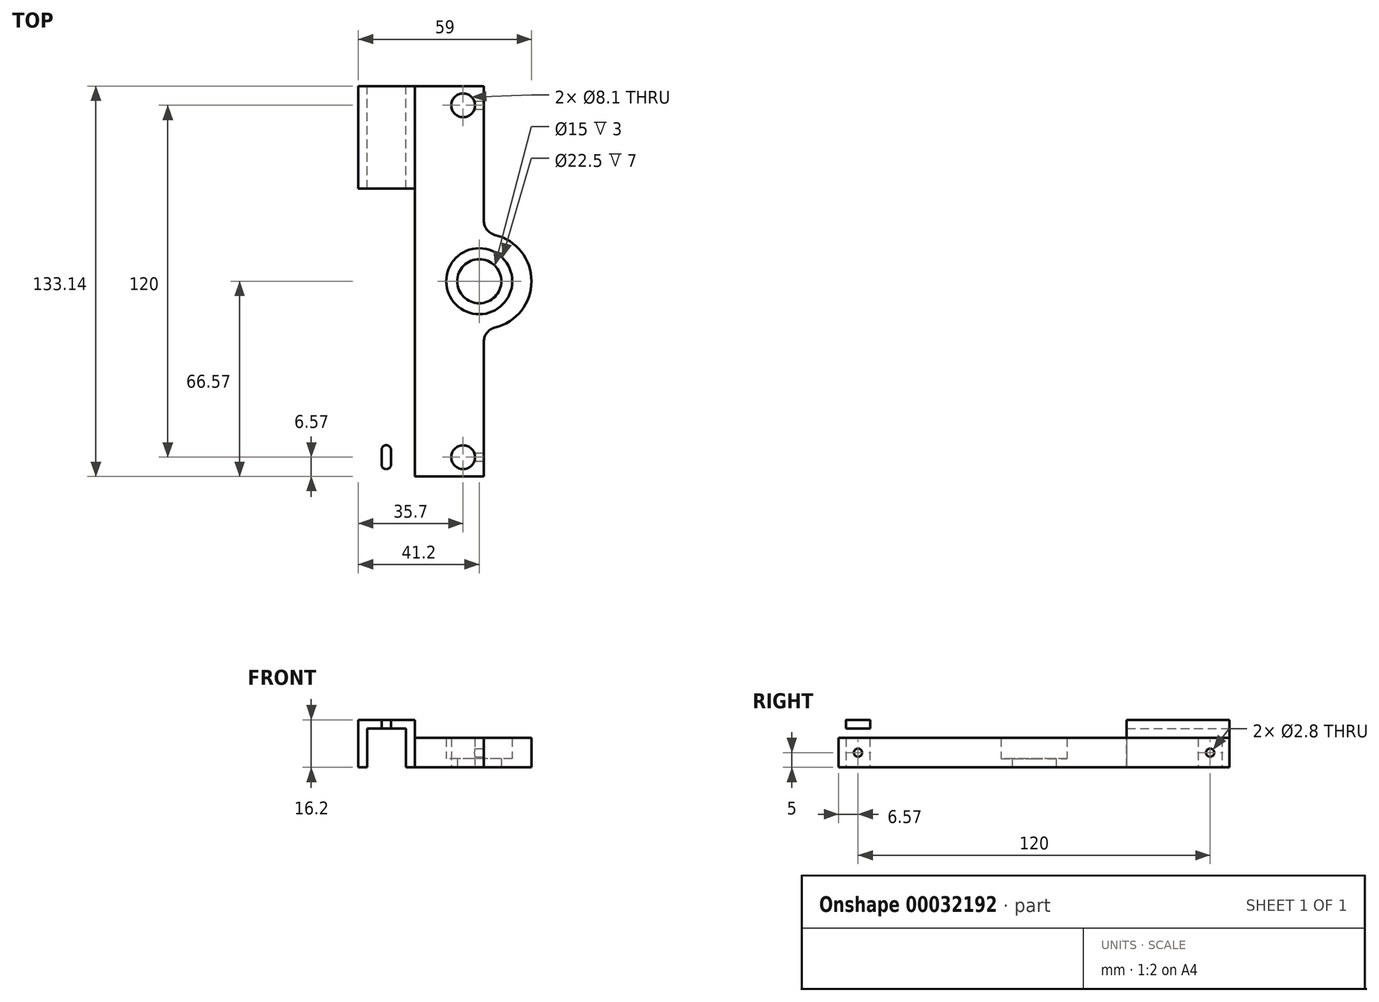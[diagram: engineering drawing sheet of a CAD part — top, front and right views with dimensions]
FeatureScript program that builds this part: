
annotation { "Feature Type Name" : "Feature", "Feature Type Description" : "" }
export const myFeature = defineFeature(function(context is Context, id is Id, definition is map)
    precondition{}
    {
        {
            var Q0;
            Q0=qCreatedBy(makeId("Top.planeOp"),FACE);
            var sketch = newSketch(context, id + "F0", { "sketchPlane" : qUnion([Q0])});
            skCircle(sketch, "E0", {"center": v(0, 0) * mm, "radius": 7.5 * mm});
            skLineSegment(sketch, "E1.rect.bottom", {"start": v(-22, -66.57) * mm, "end": v(22, -66.57) * mm});
            skLineSegment(sketch, "E1.rect.top", {"start": v(-22, 66.57) * mm, "end": v(22, 66.57) * mm});
            skLineSegment(sketch, "E1.rect.left", {"start": v(-22, -66.57) * mm, "end": v(-22, 66.57) * mm});
            skLineSegment(sketch, "E1.rect.right", {"start": v(22, -66.57) * mm, "end": v(22, 66.57) * mm});
            skCircle(sketch, "E2", {"center": v(0, 0) * mm, "radius": 11.25 * mm});
            skCircle(sketch, "E3", {"center": v(-5.5, -60) * mm, "radius": 4.05 * mm});
            skCircle(sketch, "E4", {"center": v(-5.5, 60) * mm, "radius": 4.05 * mm});
            skSolve(sketch);
        }
        {
            var Q0;
            Q0=makeQuery(id+"F0.imprint","IMPRINT",FACE,{"disambiguationData":[TD([[makeQuery(id+"F0.imprint","IMPRINT",EDGE,{"derivedFrom":sQuery(id+"F0.wireOp",EDGE,"E0")}),-1.0]])]});
            extrude(context, id + "F1", {"entities" : qUnion([Q0]), "depth" : 3 * mm});
        }
        {
            var Q0;
            Q0=makeQuery(id+"F0.imprint","IMPRINT",FACE,{"disambiguationData":[TD([[makeQuery(id+"F0.imprint","IMPRINT",EDGE,{"derivedFrom":sQuery(id+"F0.wireOp",EDGE,"E1.rect.bottom")}),1.0]])]});
            extrude(context, id + "F2", {"entities" : qUnion([Q0]), "operationType" : NewBodyOperationType.ADD, "depth" : 10 * mm});
        }
        {
            var Q0;
            Q0=makeQuery(id+"F2.opExtrude","CAP_FACE",FACE,{"disambiguationData":[OSD([sQuery(id+"F0.wireOp",EDGE,"E1.rect.bottom"),sQuery(id+"F0.wireOp",EDGE,"E1.rect.top"),sQuery(id+"F0.wireOp",EDGE,"E1.rect.left"),sQuery(id+"F0.wireOp",EDGE,"E1.rect.right"),sQuery(id+"F0.wireOp",EDGE,"E2"),sQuery(id+"F0.wireOp",EDGE,"E3"),sQuery(id+"F0.wireOp",EDGE,"E4")])],"isStart":false});
            var sketch = newSketch(context, id + "F3", { "sketchPlane" : qUnion([Q0])});
            skLineSegment(sketch, "E5", {"start": v(1.55, -66.57) * mm, "end": v(1.55, -16.25) * mm});
            skLineSegment(sketch, "E6", {"start": v(1.55, -16.25) * mm, "end": v(22, -16.25) * mm});
            skLineSegment(sketch, "E7", {"start": v(1.55, 66.57) * mm, "end": v(1.55, 16.25) * mm});
            skLineSegment(sketch, "E8", {"start": v(1.55, 16.25) * mm, "end": v(22, 16.25) * mm});
            skSolve(sketch);
        }
        {
            var Q0;
            {var subQ4=sQuery(id+"F3.wireOp",EDGE,"E5");Q0=makeQuery(id+"F3.imprint","IMPRINT",FACE,{"disambiguationData":[TD([[makeQuery(id+"F3.imprint","IMPRINT",EDGE,{"derivedFrom":subQ4}),-1.0]])]});}
            var Q1;
            {var subQ4=sQuery(id+"F3.wireOp",EDGE,"E7");Q1=makeQuery(id+"F3.imprint","IMPRINT",FACE,{"disambiguationData":[TD([[makeQuery(id+"F3.imprint","IMPRINT",EDGE,{"derivedFrom":subQ4}),1.0]])]});}
            extrude(context, id + "F4", {"entities" : qUnion([Q0, Q1]), "operationType" : NewBodyOperationType.REMOVE, "endBound" : BoundingType.UP_TO_NEXT, "oppositeDirection" : true, "depth" : 25 * mm});
        }
        {
            var Q0;
            Q0=makeQuery(id+"F2.opExtrude","CAP_FACE",FACE,{"disambiguationData":[OSD([sQuery(id+"F0.wireOp",EDGE,"E1.rect.bottom"),sQuery(id+"F0.wireOp",EDGE,"E1.rect.top"),sQuery(id+"F0.wireOp",EDGE,"E1.rect.left"),sQuery(id+"F0.wireOp",EDGE,"E1.rect.right"),sQuery(id+"F0.wireOp",EDGE,"E2"),sQuery(id+"F0.wireOp",EDGE,"E3"),sQuery(id+"F0.wireOp",EDGE,"E4")])],"isStart":false});
            var sketch = newSketch(context, id + "F5", { "sketchPlane" : qUnion([Q0])});
            skArc(sketch, "E9", {"start": v(1.55, -16.25) * mm, "mid": v(17.8, 0) * mm, "end": v(1.55, 16.25) * mm});
            skSolve(sketch);
        }
        {
            var Q0;
            Q0=makeQuery(id+"F5.imprint","IMPRINT",FACE,{"disambiguationData":[TD([[makeQuery(id+"F5.imprint","IMPRINT",EDGE,{"derivedFrom":sQuery(id+"F5.wireOp",EDGE,"E9")}),-1.0]])]});
            extrude(context, id + "F6", {"entities" : qUnion([Q0]), "operationType" : NewBodyOperationType.REMOVE, "endBound" : BoundingType.UP_TO_NEXT, "oppositeDirection" : true, "depth" : 25 * mm});
        }
        {
            var Q0;
            Q0=makeQuery(id+"F2.opExtrude","SWEPT_FACE",FACE,{"disambiguationData":[OSD([sQuery(id+"F0.wireOp",EDGE,"E1.rect.bottom")])]});
            var sketch = newSketch(context, id + "F7", { "sketchPlane" : qUnion([Q0])});
            skLineSegment(sketch, "E10", {"start": v(-22, 0) * mm, "end": v(-25, 0) * mm});
            skLineSegment(sketch, "E11", {"start": v(-25, 13.2) * mm, "end": v(-25, 0) * mm});
            skLineSegment(sketch, "E12", {"start": v(-25, 13.2) * mm, "end": v(-38.2, 13.2) * mm});
            skLineSegment(sketch, "E13", {"start": v(-38.2, 0) * mm, "end": v(-38.2, 13.2) * mm});
            skLineSegment(sketch, "E14", {"start": v(-38.2, 0) * mm, "end": v(-41.2, 0) * mm});
            skLineSegment(sketch, "E15", {"start": v(-41.2, 0) * mm, "end": v(-41.2, 16.2) * mm});
            skLineSegment(sketch, "E16", {"start": v(-41.2, 16.2) * mm, "end": v(-22, 16.2) * mm});
            skLineSegment(sketch, "E17", {"start": v(-22, 16.2) * mm, "end": v(-22, 0) * mm});
            skSolve(sketch);
        }
        {
            var Q0;
            Q0 = qSketchRegion(id + "F7", true);
            var Q1;
            Q1=makeQuery(id+"F7.imprint","IMPRINT",FACE,{"disambiguationData":[TD([[makeQuery(id+"F7.imprint","IMPRINT",EDGE,{"derivedFrom":sQuery(id+"F7.wireOp",EDGE,"E10")}),-1.0]])]});
            var Q2;
            Q2=makeQuery(id+"F2.opExtrude","SWEPT_FACE",FACE,{"disambiguationData":[OSD([sQuery(id+"F0.wireOp",EDGE,"E1.rect.top")])]});
            extrude(context, id + "F8", {"entities" : qUnion([Q0, Q1]), "operationType" : NewBodyOperationType.ADD, "oppositeDirection" : true, "endBoundEntityFace" : qUnion([Q2]), "depth" : 35 * mm});
        }
        {
            var Q0;
            Q0=makeQuery(id+"F2.opExtrude","SWEPT_FACE",FACE,{"disambiguationData":[OSD([sQuery(id+"F0.wireOp",EDGE,"E1.rect.top")])]});
            var sketch = newSketch(context, id + "F9", { "sketchPlane" : qUnion([Q0])});
            skLineSegment(sketch, "E18.0.0", {"start": v(25, 0) * mm, "end": v(3.45, 0) * mm});
            skLineSegment(sketch, "E18.0.1", {"start": v(3.45, 0) * mm, "end": v(3.45, 10) * mm});
            skLineSegment(sketch, "E18.0.2", {"start": v(3.45, 10) * mm, "end": v(22, 10) * mm});
            skLineSegment(sketch, "E18.0.3", {"start": v(22, 10) * mm, "end": v(22, 16.2) * mm});
            skLineSegment(sketch, "E18.0.4", {"start": v(22, 16.2) * mm, "end": v(41.2, 16.2) * mm});
            skLineSegment(sketch, "E18.0.5", {"start": v(41.2, 16.2) * mm, "end": v(41.2, 0) * mm});
            skLineSegment(sketch, "E18.0.6", {"start": v(41.2, 0) * mm, "end": v(38.2, 0) * mm});
            skLineSegment(sketch, "E18.0.7", {"start": v(38.2, 0) * mm, "end": v(38.2, 13.2) * mm});
            skLineSegment(sketch, "E18.0.8", {"start": v(38.2, 13.2) * mm, "end": v(25, 13.2) * mm});
            skLineSegment(sketch, "E18.0.9", {"start": v(25, 13.2) * mm, "end": v(25, 0) * mm});
            skSolve(sketch);
        }
        {
            var Q0;
            Q0=makeQuery(id+"F9.imprint","IMPRINT",FACE,{"disambiguationData":[TD([[makeQuery(id+"F9.imprint","IMPRINT",EDGE,{"derivedFrom":sQuery(id+"F9.wireOp",EDGE,"E18.0.3")}),-1.0]])]});
            extrude(context, id + "F10", {"entities" : qUnion([Q0]), "operationType" : NewBodyOperationType.ADD, "oppositeDirection" : true, "depth" : 35 * mm});
        }
        {
            var Q0;
            Q0=makeQuery(id+"F8.opExtrude","SWEPT_FACE",FACE,{"disambiguationData":[OSD([sQuery(id+"F7.wireOp",EDGE,"E16")])]});
            var sketch = newSketch(context, id + "F11", { "sketchPlane" : qUnion([Q0])});
            skArc(sketch, "E19.0.startCap", {"start": v(-30.1, -62.5) * mm, "mid": v(-31.7, -64.1) * mm, "end": v(-33.3, -62.5) * mm});
            skArc(sketch, "E19.0.endCap", {"start": v(-33.3, -57.5) * mm, "mid": v(-31.7, -55.9) * mm, "end": v(-30.1, -57.5) * mm});
            skLineSegment(sketch, "E19.0.left", {"start": v(-33.3, -62.5) * mm, "end": v(-33.3, -57.5) * mm});
            skLineSegment(sketch, "E19.0.right", {"start": v(-30.1, -62.5) * mm, "end": v(-30.1, -57.5) * mm});
            skArc(sketch, "E20.0.startCap", {"start": v(-30.1, 57.5) * mm, "mid": v(-31.7, 55.9) * mm, "end": v(-33.3, 57.5) * mm});
            skLineSegment(sketch, "E20.0.left", {"start": v(-33.3, 57.5) * mm, "end": v(-33.3, 62.5) * mm});
            skLineSegment(sketch, "E20.0.right", {"start": v(-30.1, 57.5) * mm, "end": v(-30.1, 62.5) * mm});
            skArc(sketch, "E20.0.endCap", {"start": v(-33.3, 62.5) * mm, "mid": v(-31.7, 64.1) * mm, "end": v(-30.1, 62.5) * mm});
            skSolve(sketch);
        }
        {
            var Q0;
            Q0=makeQuery(id+"F11.imprint","IMPRINT",FACE,{"disambiguationData":[TD([[makeQuery(id+"F11.imprint","IMPRINT",EDGE,{"derivedFrom":sQuery(id+"F11.wireOp",EDGE,"E19.0.startCap")}),-1.0]])]});
            var Q1;
            Q1=makeQuery(id+"F11.imprint","IMPRINT",FACE,{"disambiguationData":[TD([[makeQuery(id+"F11.imprint","IMPRINT",EDGE,{"derivedFrom":sQuery(id+"F11.wireOp",EDGE,"E20.0.startCap")}),-1.0]])]});
            var Q2;
            Q2=sQuery(id+"F11.wireOp",EDGE,"E19.0.startCap");
            var Q3;
            Q3=sQuery(id+"F11.wireOp",EDGE,"E19.0.left");
            var Q4;
            Q4=sQuery(id+"F11.wireOp",EDGE,"E19.0.right");
            var Q5;
            Q5=sQuery(id+"F11.wireOp",EDGE,"E19.0.endCap");
            extrude(context, id + "F12", {"entities" : qUnion([Q0, Q1]), "operationType" : NewBodyOperationType.REMOVE, "surfaceEntities" : qUnion([Q2, Q3, Q4, Q5]), "endBound" : BoundingType.THROUGH_ALL, "oppositeDirection" : true, "depth" : 25 * mm});
        }
        {
            var Q0;
            Q0=makeQuery(id+"F4.boolean.opBoolean","COPY",FACE,{"derivedFrom":makeQuery(id+"F4.opExtrude","SWEPT_FACE",FACE,{"disambiguationData":[OSD([sQuery(id+"F3.wireOp",EDGE,"E5")])]})});
            var sketch = newSketch(context, id + "F13", { "sketchPlane" : qUnion([Q0])});
            skCircle(sketch, "E21", {"center": v(-60, 5) * mm, "radius": 1.4 * mm});
            skPoint(sketch, "E21.centerSnap0", {"position": v(-66.57, 5) * mm});
            skCircle(sketch, "E22", {"center": v(60, 5) * mm, "radius": 1.4 * mm});
            skSolve(sketch);
        }
        {
            var Q0;
            Q0=makeQuery(id+"F13.imprint","IMPRINT",FACE,{"disambiguationData":[TD([[makeQuery(id+"F13.imprint","IMPRINT",EDGE,{"derivedFrom":sQuery(id+"F13.wireOp",EDGE,"E21")}),1.0]])]});
            var Q1;
            Q1=makeQuery(id+"F13.imprint","IMPRINT",FACE,{"disambiguationData":[TD([[makeQuery(id+"F13.imprint","IMPRINT",EDGE,{"derivedFrom":sQuery(id+"F13.wireOp",EDGE,"E22")}),1.0]])]});
            var Q2;
            Q2=makeQuery(id+"F1.opExtrude","SWEPT_BODY",BODY,{"disambiguationData":[OSD([sQuery(id+"F0.wireOp",EDGE,"E0"),sQuery(id+"F0.wireOp",EDGE,"E2")])]});
            extrude(context, id + "F14", {"entities" : qUnion([Q0, Q1]), "operationType" : NewBodyOperationType.REMOVE, "endBound" : BoundingType.UP_TO_BODY, "oppositeDirection" : true, "endBoundEntityBody" : qUnion([Q2]), "depth" : 25 * mm});
        }
        {
            var Q0;
            Q0=makeQuery(id+"F4.boolean.opBoolean","COPY",EDGE,{"derivedFrom":makeQuery(id+"F4.opExtrude","SWEPT_EDGE",EDGE,{"disambiguationData":[OSD([sQuery(id+"F0.wireOp",EDGE,"E1.rect.top"),sQuery(id+"F3.wireOp",EDGE,"E7")])]})});
            var Q1;
            Q1=makeQuery(id+"F4.boolean.opBoolean","COPY",EDGE,{"derivedFrom":makeQuery(id+"F4.opExtrude","SWEPT_EDGE",EDGE,{"disambiguationData":[OSD([sQuery(id+"F0.wireOp",EDGE,"E1.rect.bottom"),sQuery(id+"F3.wireOp",EDGE,"E5")])]})});
            var Q2;
            {var subQ0=sQuery(id+"F3.wireOp",EDGE,"E5");var subQ1=sQuery(id+"F3.wireOp",EDGE,"E6");Q2=makeQuery(id+"F6.boolean.opBoolean","MERGE",EDGE,{"derivedFrom":[makeQuery(id+"F4.boolean.opBoolean","COPY",EDGE,{"derivedFrom":makeQuery(id+"F4.opExtrude","SWEPT_EDGE",EDGE,{"disambiguationData":[OSD([subQ0,subQ1])]})}),makeQuery(id+"F6.opExtrude","SWEPT_EDGE",EDGE,{"disambiguationData":[OSD([subQ0,subQ1,sQuery(id+"F5.wireOp",EDGE,"E9")])]})]});}
            var Q3;
            {var subQ0=sQuery(id+"F3.wireOp",EDGE,"E7");var subQ1=sQuery(id+"F3.wireOp",EDGE,"E8");Q3=makeQuery(id+"F6.boolean.opBoolean","MERGE",EDGE,{"derivedFrom":[makeQuery(id+"F4.boolean.opBoolean","COPY",EDGE,{"derivedFrom":makeQuery(id+"F4.opExtrude","SWEPT_EDGE",EDGE,{"disambiguationData":[OSD([subQ0,subQ1])]})}),makeQuery(id+"F6.opExtrude","SWEPT_EDGE",EDGE,{"disambiguationData":[OSD([sQuery(id+"F0.wireOp",EDGE,"E0"),sQuery(id+"F0.wireOp",EDGE,"E1.rect.bottom"),sQuery(id+"F0.wireOp",EDGE,"E1.rect.top"),sQuery(id+"F0.wireOp",EDGE,"E1.rect.left"),sQuery(id+"F0.wireOp",EDGE,"E1.rect.right"),sQuery(id+"F0.wireOp",EDGE,"E2"),sQuery(id+"F0.wireOp",EDGE,"E3"),sQuery(id+"F0.wireOp",EDGE,"E4"),subQ0,subQ1])]})]});}
            fillet(context, id + "F15", {"entities" : qUnion([Q0, Q1, Q2, Q3]), "radius" : 5 * mm, "tangentPropagation" : true, "allowEdgeOverflow" : false});
        }
    });
